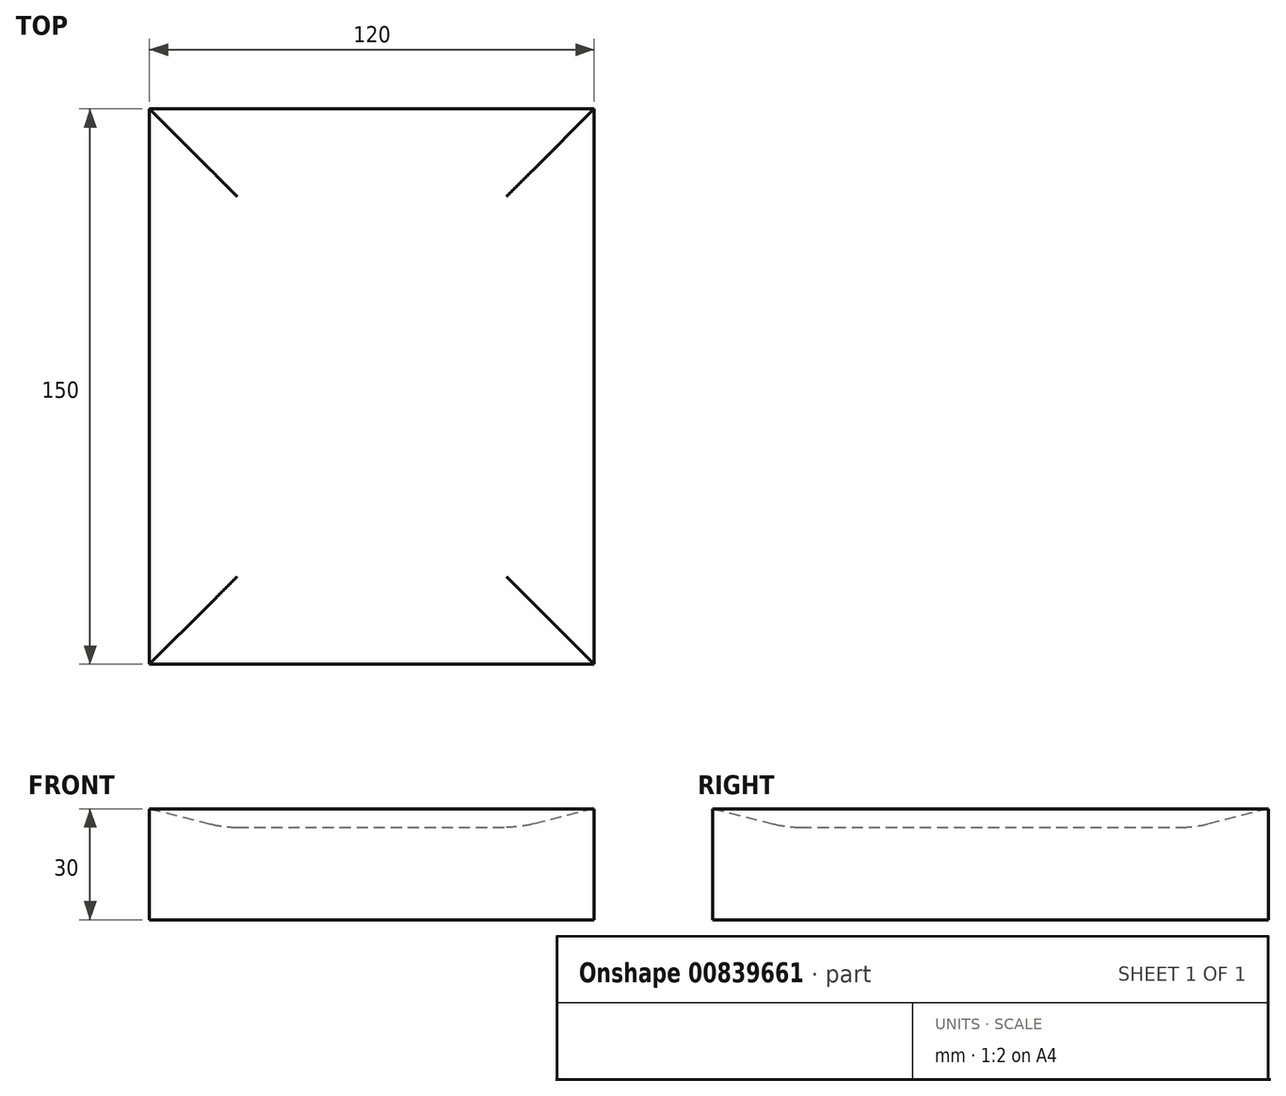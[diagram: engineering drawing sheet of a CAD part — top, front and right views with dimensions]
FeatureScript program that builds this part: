
annotation { "Feature Type Name" : "Feature", "Feature Type Description" : "" }
export const myFeature = defineFeature(function(context is Context, id is Id, definition is map)
    precondition{}
    {
        {
            var Q0;
            Q0=qCreatedBy(makeId("Top.planeOp"),FACE);
            var sketch = newSketch(context, id + "F0", { "sketchPlane" : qUnion([Q0])});
            skLineSegment(sketch, "E0.bottom", {"start": v(0, 0) * mm, "end": v(120, 0) * mm});
            skLineSegment(sketch, "E0.top", {"start": v(0, 150) * mm, "end": v(120, 150) * mm});
            skLineSegment(sketch, "E0.left", {"start": v(0, 0) * mm, "end": v(0, 150) * mm});
            skLineSegment(sketch, "E0.right", {"start": v(120, 0) * mm, "end": v(120, 150) * mm});
            skSolve(sketch);
        }
        {
            var Q0;
            Q0 = qSketchRegion(id + "F0", true);
            extrude(context, id + "F1", {"entities" : qUnion([Q0]), "depth" : 30 * mm, "offsetDistance" : 25 * mm});
        }
        {
            var Q0;
            Q0=qCreatedBy(makeId("Top.planeOp"),FACE);
            cPlane(context, id + "F2", {"entities" : qUnion([Q0]), "cplaneType" : CPlaneType.OFFSET, "offset" : 25 * mm, "width" : 150 * mm, "height" : 150 * mm});
        }
        {
            var Q0;
            Q0=qCreatedBy(id+"F2.planeOp",FACE);
            var sketch = newSketch(context, id + "F3", { "sketchPlane" : qUnion([Q0])});
            skLineSegment(sketch, "E1.bottom", {"start": v(20, 130) * mm, "end": v(100, 130) * mm});
            skLineSegment(sketch, "E1.top", {"start": v(20, 20) * mm, "end": v(100, 20) * mm});
            skLineSegment(sketch, "E1.left", {"start": v(20, 130) * mm, "end": v(20, 20) * mm});
            skLineSegment(sketch, "E1.right", {"start": v(100, 130) * mm, "end": v(100, 20) * mm});
            skSolve(sketch);
        }
        {
            var Q1;
            Q1=makeQuery(id+"F1.opExtrude","CAP_FACE",FACE,{"disambiguationData":[OSD([sQuery(id+"F0.wireOp",EDGE,"E0.bottom"),sQuery(id+"F0.wireOp",EDGE,"E0.top"),sQuery(id+"F0.wireOp",EDGE,"E0.left"),sQuery(id+"F0.wireOp",EDGE,"E0.right")])],"isStart":false});
            var Q2;
            Q2 = qSketchRegion(id + "F3", true);
            loft(context, id + "F4", {"operationType" : NewBodyOperationType.REMOVE, "sheetProfilesArray" : [{ "sheetProfileEntities" : qUnion([Q1]) }, { "sheetProfileEntities" : qUnion([Q2]) }]});
        }
        {
            var Q0;
            Q0=makeQuery(id+"F4.boolean.opBoolean","COPY",EDGE,{"derivedFrom":makeQuery(id+"F4.opLoft","MID_CAP_EDGE",EDGE,{"disambiguationData":[OSD([sQuery(id+"F3.wireOp",EDGE,"E1.bottom"),sQuery(id+"F3.wireOp",EDGE,"E1.top"),sQuery(id+"F3.wireOp",EDGE,"E1.left")])],"capPos":1.0})});
            var Q1;
            Q1=makeQuery(id+"F4.boolean.opBoolean","COPY",EDGE,{"derivedFrom":makeQuery(id+"F4.opLoft","MID_CAP_EDGE",EDGE,{"disambiguationData":[OSD([sQuery(id+"F3.wireOp",EDGE,"E1.top"),sQuery(id+"F3.wireOp",EDGE,"E1.left"),sQuery(id+"F3.wireOp",EDGE,"E1.right")])],"capPos":1.0})});
            var Q2;
            Q2=makeQuery(id+"F4.boolean.opBoolean","COPY",EDGE,{"derivedFrom":makeQuery(id+"F4.opLoft","MID_CAP_EDGE",EDGE,{"disambiguationData":[OSD([sQuery(id+"F3.wireOp",EDGE,"E1.bottom"),sQuery(id+"F3.wireOp",EDGE,"E1.top"),sQuery(id+"F3.wireOp",EDGE,"E1.right")])],"capPos":1.0})});
            var Q3;
            Q3=makeQuery(id+"F4.boolean.opBoolean","COPY",EDGE,{"derivedFrom":makeQuery(id+"F4.opLoft","MID_CAP_EDGE",EDGE,{"disambiguationData":[OSD([sQuery(id+"F3.wireOp",EDGE,"E1.bottom"),sQuery(id+"F3.wireOp",EDGE,"E1.left"),sQuery(id+"F3.wireOp",EDGE,"E1.right")])],"capPos":1.0})});
            fillet(context, id + "F5", {"entities" : qUnion([Q0, Q1, Q2, Q3]), "radius" : 30 * mm, "tangentPropagation" : true, "allowEdgeOverflow" : false});
        }
    });
